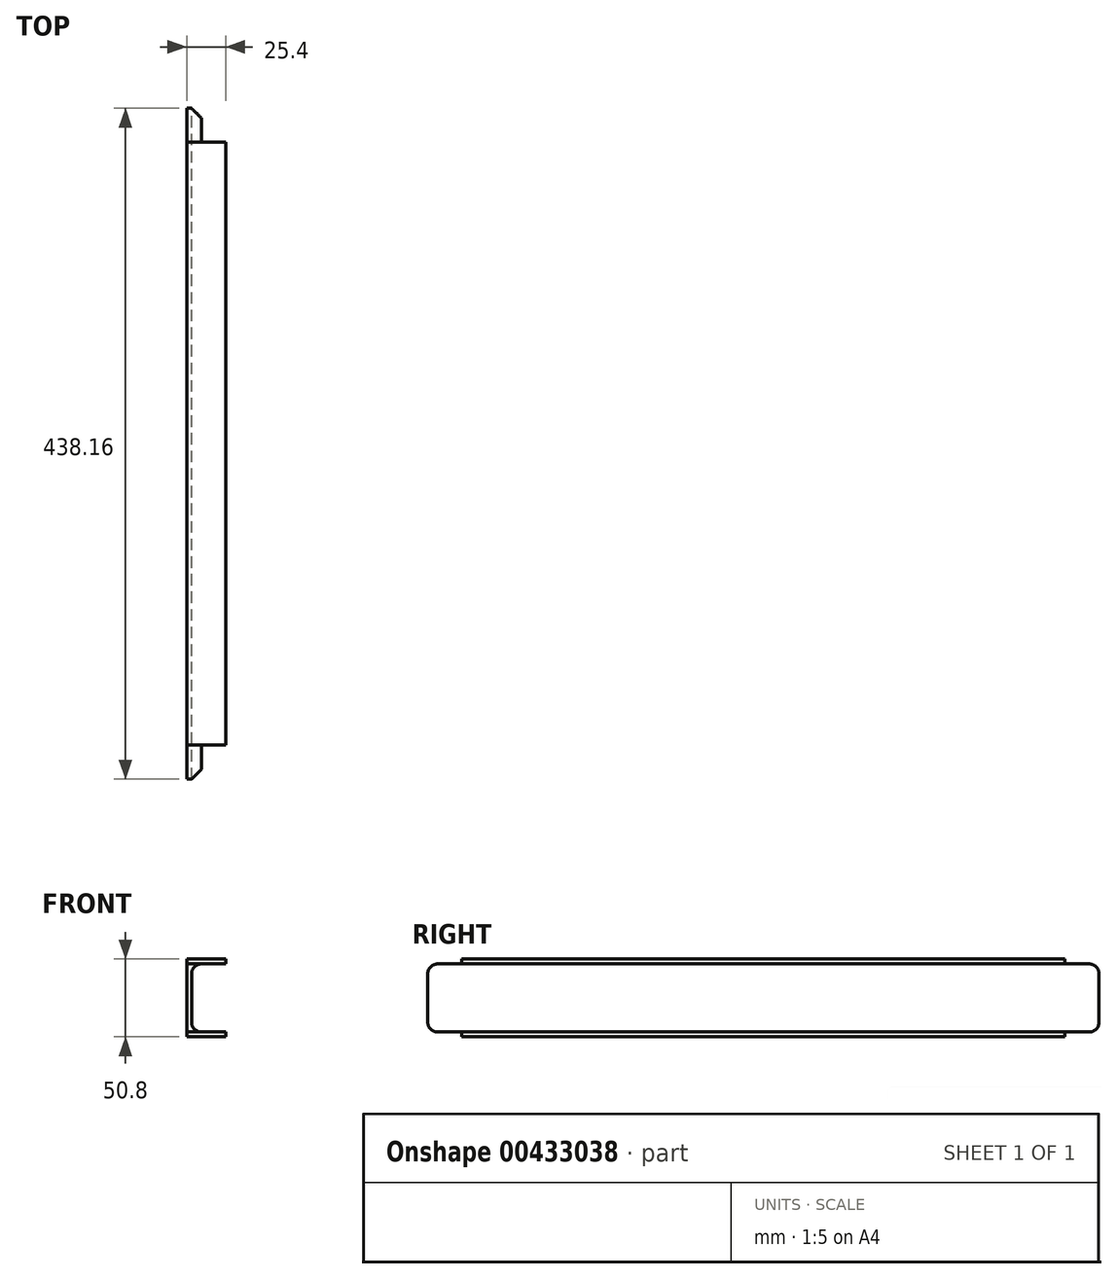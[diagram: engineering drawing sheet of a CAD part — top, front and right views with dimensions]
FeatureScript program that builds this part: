
annotation { "Feature Type Name" : "Feature", "Feature Type Description" : "" }
export const myFeature = defineFeature(function(context is Context, id is Id, definition is map)
    precondition{}
    {
        {
            var Q0;
            Q0=qCreatedBy(makeId("Front.planeOp"),FACE);
            var sketch = newSketch(context, id + "F0", { "sketchPlane" : qUnion([Q0])});
            skLineSegment(sketch, "E0", {"start": v(0, 0) * mm, "end": v(0, 50.8) * mm});
            skLineSegment(sketch, "E1", {"start": v(0, 50.8) * mm, "end": v(25.4, 50.8) * mm});
            skLineSegment(sketch, "E2", {"start": v(25.4, 50.8) * mm, "end": v(25.4, 47.63) * mm});
            skLineSegment(sketch, "E3", {"start": v(25.4, 47.63) * mm, "end": v(9.52, 47.62) * mm});
            skLineSegment(sketch, "E4", {"start": v(3.17, 41.27) * mm, "end": v(3.18, 9.52) * mm});
            skLineSegment(sketch, "E5", {"start": v(9.53, 3.17) * mm, "end": v(25.4, 3.18) * mm});
            skLineSegment(sketch, "E6", {"start": v(25.4, 3.18) * mm, "end": v(25.4, 0) * mm});
            skLineSegment(sketch, "E7", {"start": v(25.4, 0) * mm, "end": v(0, 0) * mm});
            skPoint(sketch, "E8.visualSharp", {"position": v(3.17, 47.63) * mm});
            skArc(sketch, "E8.filletArc", {"start": v(9.52, 47.62) * mm, "mid": v(5.03, 45.77) * mm, "end": v(3.17, 41.27) * mm});
            skPoint(sketch, "E9.visualSharp", {"position": v(3.18, 3.17) * mm});
            skArc(sketch, "E9.filletArc", {"start": v(3.18, 9.53) * mm, "mid": v(5.03, 5.03) * mm, "end": v(9.53, 3.17) * mm});
            skSolve(sketch);
        }
        {
            var Q0;
            Q0=makeQuery(id+"F0.imprint","IMPRINT",FACE,{"disambiguationData":[TD([[makeQuery(id+"F0.imprint","IMPRINT",EDGE,{"derivedFrom":sQuery(id+"F0.wireOp",EDGE,"E0")}),-1.0]])]});
            extrude(context, id + "F1", {"entities" : qUnion([Q0]), "depth" : 444.5 * mm, "offsetDistance" : 25.4 * mm});
        }
        {
            var Q0;
            Q0=qCreatedBy(makeId("Right.planeOp"),FACE);
            var sketch = newSketch(context, id + "F2", { "sketchPlane" : qUnion([Q0])});
            skLineSegment(sketch, "E10", {"start": v(0, 0) * mm, "end": v(0, 50.8) * mm});
            skLineSegment(sketch, "E11", {"start": v(0, 50.8) * mm, "end": v(-25.4, 50.8) * mm});
            skLineSegment(sketch, "E12", {"start": v(-25.4, 50.8) * mm, "end": v(-25.4, 47.62) * mm});
            skLineSegment(sketch, "E13", {"start": v(-25.4, 47.63) * mm, "end": v(-9.53, 47.63) * mm});
            skLineSegment(sketch, "E14", {"start": v(-3.18, 41.28) * mm, "end": v(-3.17, 9.53) * mm});
            skLineSegment(sketch, "E15", {"start": v(-9.52, 3.18) * mm, "end": v(-25.4, 3.17) * mm});
            skLineSegment(sketch, "E16", {"start": v(-25.4, 3.17) * mm, "end": v(-25.4, 0) * mm});
            skLineSegment(sketch, "E17", {"start": v(-25.4, 0) * mm, "end": v(0, 0) * mm});
            skPoint(sketch, "E18.visualSharp", {"position": v(-3.18, 47.63) * mm});
            skArc(sketch, "E18.filletArc", {"start": v(-3.18, 41.28) * mm, "mid": v(-5.03, 45.77) * mm, "end": v(-9.53, 47.63) * mm});
            skPoint(sketch, "E19.visualSharp", {"position": v(-3.17, 3.18) * mm});
            skArc(sketch, "E19.filletArc", {"start": v(-9.52, 3.17) * mm, "mid": v(-5.03, 5.03) * mm, "end": v(-3.17, 9.53) * mm});
            skLineSegment(sketch, "E20", {"start": v(-444.5, 0) * mm, "end": v(-419.1, 0) * mm});
            skLineSegment(sketch, "E21", {"start": v(-419.1, 0) * mm, "end": v(-419.1, 3.17) * mm});
            skLineSegment(sketch, "E22", {"start": v(-419.1, 3.18) * mm, "end": v(-434.98, 3.17) * mm});
            skLineSegment(sketch, "E23", {"start": v(-441.33, 9.52) * mm, "end": v(-441.33, 41.27) * mm});
            skLineSegment(sketch, "E24", {"start": v(-434.98, 47.62) * mm, "end": v(-419.1, 47.62) * mm});
            skLineSegment(sketch, "E25", {"start": v(-419.1, 47.62) * mm, "end": v(-419.1, 50.8) * mm});
            skLineSegment(sketch, "E26", {"start": v(-419.1, 50.8) * mm, "end": v(-444.5, 50.8) * mm});
            skLineSegment(sketch, "E27", {"start": v(-444.5, 50.8) * mm, "end": v(-444.5, 0) * mm});
            skPoint(sketch, "E28.visualSharp", {"position": v(-441.33, 3.17) * mm});
            skArc(sketch, "E28.filletArc", {"start": v(-441.33, 9.52) * mm, "mid": v(-439.47, 5.03) * mm, "end": v(-434.98, 3.17) * mm});
            skPoint(sketch, "E29.visualSharp", {"position": v(-441.33, 47.62) * mm});
            skArc(sketch, "E29.filletArc", {"start": v(-434.98, 47.62) * mm, "mid": v(-439.47, 45.77) * mm, "end": v(-441.33, 41.27) * mm});
            skSolve(sketch);
        }
        {
            var Q0;
            Q0=makeQuery(id+"F2.imprint","IMPRINT",FACE,{"disambiguationData":[TD([[makeQuery(id+"F2.imprint","IMPRINT",EDGE,{"derivedFrom":sQuery(id+"F2.wireOp",EDGE,"E10")}),1.0]])]});
            var Q1;
            Q1=makeQuery(id+"F2.imprint","IMPRINT",FACE,{"disambiguationData":[TD([[makeQuery(id+"F2.imprint","IMPRINT",EDGE,{"derivedFrom":sQuery(id+"F2.wireOp",EDGE,"E20")}),1.0]])]});
            extrude(context, id + "F3", {"entities" : qUnion([Q0, Q1]), "operationType" : NewBodyOperationType.REMOVE, "endBound" : BoundingType.THROUGH_ALL, "depth" : 25.4 * mm});
        }
    });
